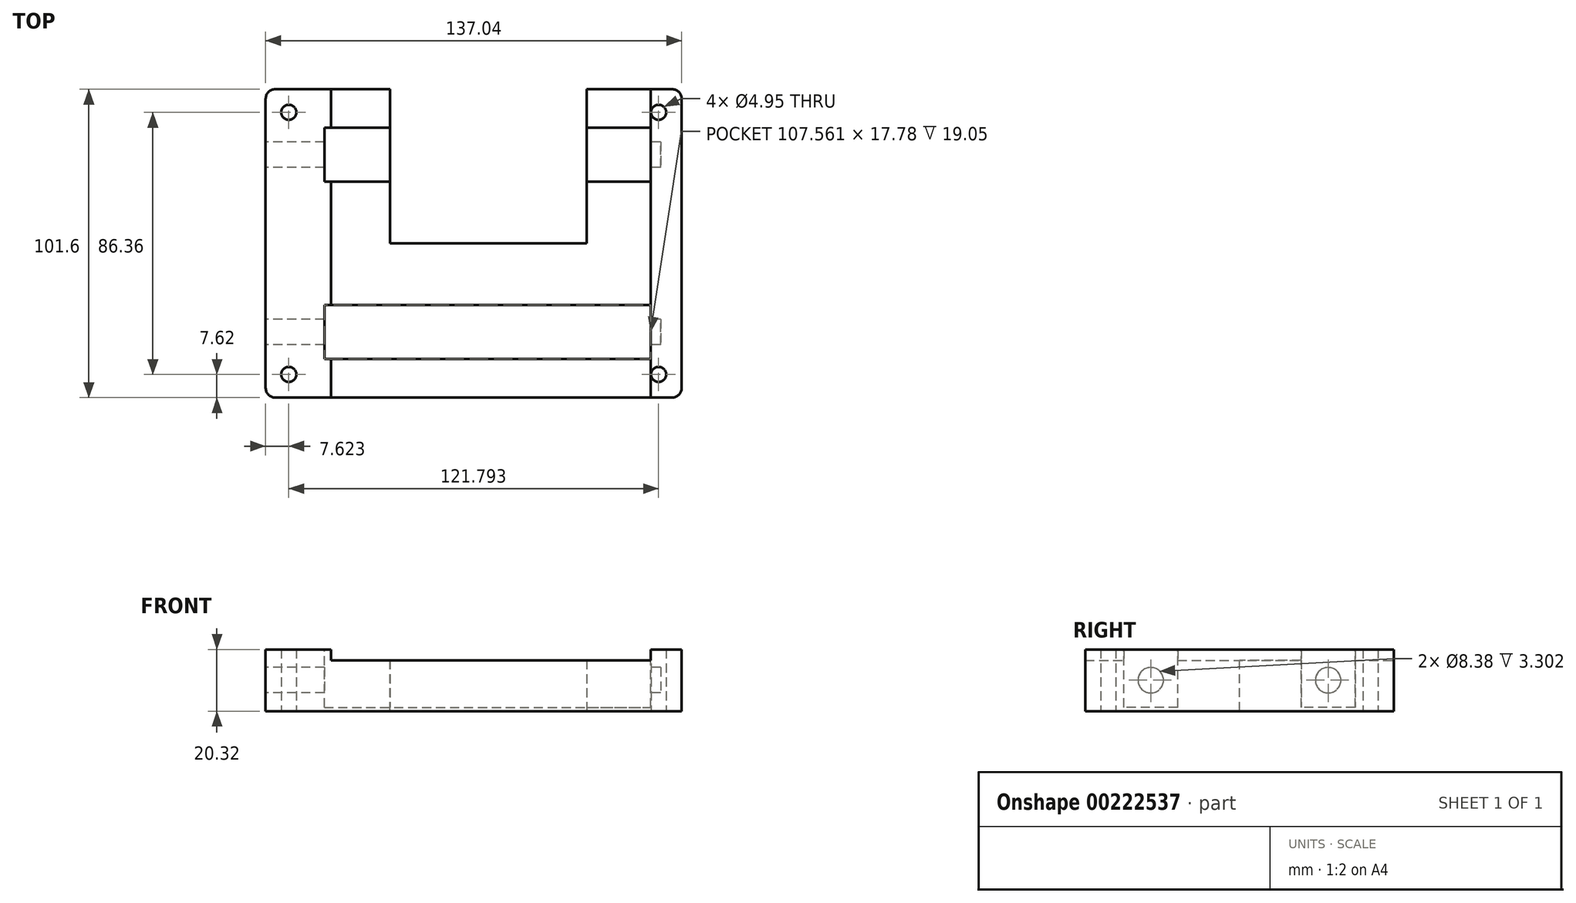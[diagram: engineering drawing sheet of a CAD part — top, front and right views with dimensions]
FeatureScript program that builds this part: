
annotation { "Feature Type Name" : "Feature", "Feature Type Description" : "" }
export const myFeature = defineFeature(function(context is Context, id is Id, definition is map)
    precondition{}
    {
        {
            var Q0;
            Q0=qCreatedBy(makeId("Right.planeOp"),FACE);
            cPlane(context, id + "F0", {"entities" : qUnion([Q0]), "cplaneType" : CPlaneType.OFFSET, "offset" : 4.83 * mm, "width" : 152.4 * mm, "height" : 152.4 * mm});
        }
        {
            var Q0;
            Q0=qCreatedBy(makeId("Top.planeOp"),FACE);
            var sketch = newSketch(context, id + "F1", { "sketchPlane" : qUnion([Q0])});
            skLineSegment(sketch, "E0", {"start": v(0, 50.8) * mm, "end": v(-68.52, 50.8) * mm});
            skLineSegment(sketch, "E1", {"start": v(-68.52, 50.8) * mm, "end": v(-68.52, 0) * mm});
            skLineSegment(sketch, "E2.MirrorCS", {"start": v(0, 50.8) * mm, "end": v(68.52, 50.8) * mm});
            skLineSegment(sketch, "E3.MirrorCS", {"start": v(68.52, 50.8) * mm, "end": v(68.52, 0) * mm});
            skLineSegment(sketch, "E4.MirrorCS", {"start": v(0, -50.8) * mm, "end": v(-68.52, -50.8) * mm});
            skLineSegment(sketch, "E5.MirrorCS", {"start": v(0, -50.8) * mm, "end": v(68.52, -50.8) * mm});
            skLineSegment(sketch, "E6.MirrorCS", {"start": v(68.52, -50.8) * mm, "end": v(68.52, 0) * mm});
            skLineSegment(sketch, "E7.MirrorCS", {"start": v(-68.52, -50.8) * mm, "end": v(-68.52, 0) * mm});
            skCircle(sketch, "E8", {"center": v(-60.9, 43.18) * mm, "radius": 2.48 * mm});
            skCircle(sketch, "E9.MirrorC", {"center": v(60.9, 43.18) * mm, "radius": 2.48 * mm});
            skCircle(sketch, "E10.MirrorC", {"center": v(-60.9, -43.18) * mm, "radius": 2.48 * mm});
            skCircle(sketch, "E11.MirrorC", {"center": v(60.9, -43.18) * mm, "radius": 2.48 * mm});
            skSolve(sketch);
        }
        {
            var Q0;
            Q0 = qSketchRegion(id + "F1", true);
            extrude(context, id + "F2", {"entities" : qUnion([Q0]), "depth" : 20.32 * mm});
        }
        {
            var Q0;
            Q0=makeQuery(id+"F2.opExtrude","SWEPT_FACE",FACE,{"disambiguationData":[OSD([sQuery(id+"F1.wireOp",EDGE,"E0"),sQuery(id+"F1.wireOp",EDGE,"E2.MirrorCS")])]});
            var sketch = newSketch(context, id + "F3", { "sketchPlane" : qUnion([Q0])});
            skLineSegment(sketch, "E12.bottom", {"start": v(-58.36, 20.32) * mm, "end": v(0, 20.32) * mm});
            skLineSegment(sketch, "E12.top", {"start": v(-58.36, 16.76) * mm, "end": v(0, 16.76) * mm});
            skLineSegment(sketch, "E12.left", {"start": v(-58.36, 20.32) * mm, "end": v(-58.36, 16.76) * mm});
            skLineSegment(sketch, "E12.right", {"start": v(0, 20.32) * mm, "end": v(0, 16.76) * mm});
            skLineSegment(sketch, "E13.bottom", {"start": v(0, 20.32) * mm, "end": v(47.04, 20.32) * mm});
            skLineSegment(sketch, "E13.top", {"start": v(0, 16.76) * mm, "end": v(47.04, 16.76) * mm});
            skLineSegment(sketch, "E13.right", {"start": v(47.04, 20.32) * mm, "end": v(47.04, 16.76) * mm});
            skSolve(sketch);
        }
        {
            var Q0;
            Q0 = qSketchRegion(id + "F3", true);
            extrude(context, id + "F4", {"entities" : qUnion([Q0]), "operationType" : NewBodyOperationType.REMOVE, "oppositeDirection" : true, "depth" : 131.57 * mm});
        }
        {
            var Q0;
            Q0=makeQuery(id+"F2.opExtrude","SWEPT_EDGE",EDGE,{"disambiguationData":[OSD([sQuery(id+"F1.wireOp",EDGE,"E2.MirrorCS"),sQuery(id+"F1.wireOp",EDGE,"E3.MirrorCS")])]});
            var Q1;
            Q1=makeQuery(id+"F2.opExtrude","SWEPT_EDGE",EDGE,{"disambiguationData":[OSD([sQuery(id+"F1.wireOp",EDGE,"E0"),sQuery(id+"F1.wireOp",EDGE,"E1")])]});
            var Q2;
            Q2=makeQuery(id+"F2.opExtrude","SWEPT_EDGE",EDGE,{"disambiguationData":[OSD([sQuery(id+"F1.wireOp",EDGE,"E4.MirrorCS"),sQuery(id+"F1.wireOp",EDGE,"E7.MirrorCS")])]});
            var Q3;
            Q3=makeQuery(id+"F2.opExtrude","SWEPT_EDGE",EDGE,{"disambiguationData":[OSD([sQuery(id+"F1.wireOp",EDGE,"E5.MirrorCS"),sQuery(id+"F1.wireOp",EDGE,"E6.MirrorCS")])]});
            fillet(context, id + "F5", {"entities" : qUnion([Q0, Q1, Q2, Q3]), "radius" : 3.17 * mm, "tangentPropagation" : true, "allowEdgeOverflow" : false});
        }
        {
            var Q0;
            Q0=qCreatedBy(id+"F0.planeOp",FACE);
            var sketch = newSketch(context, id + "F6", { "sketchPlane" : qUnion([Q0])});
            skLineSegment(sketch, "E14", {"start": v(0, 53) * mm, "end": v(0, 27.48) * mm});
            skLineSegment(sketch, "E15", {"start": v(62.4, 0) * mm, "end": v(62.4, 27.48) * mm});
            skLineSegment(sketch, "E16", {"start": v(0, 0) * mm, "end": v(62.4, 0) * mm});
            skLineSegment(sketch, "E17", {"start": v(0, 0) * mm, "end": v(0, 27.48) * mm});
            skLineSegment(sketch, "E18.trimOffspring", {"start": v(0, 0) * mm, "end": v(0, -46.74) * mm});
            skLineSegment(sketch, "E19", {"start": v(0, 27.48) * mm, "end": v(62.4, 27.48) * mm});
            skSolve(sketch);
        }
        {
            var Q0;
            Q0 = qSketchRegion(id + "F6", true);
            extrude(context, id + "F7", {"entities" : qUnion([Q0]), "operationType" : NewBodyOperationType.REMOVE, "endBound" : BoundingType.SYMMETRIC, "oppositeDirection" : true, "depth" : 64.77 * mm});
        }
        {
            var Q0;
            {var subQ0=sQuery(id+"F1.wireOp",EDGE,"E2.MirrorCS");var subQ1=sQuery(id+"F1.wireOp",EDGE,"E0");var subQ2=sQuery(id+"F1.wireOp",EDGE,"E7.MirrorCS");var subQ3=sQuery(id+"F1.wireOp",EDGE,"E1");var subQ4=sQuery(id+"F1.wireOp",EDGE,"E5.MirrorCS");var subQ5=sQuery(id+"F1.wireOp",EDGE,"E4.MirrorCS");Q0=makeQuery(id+"F4.boolean.opBoolean","SPLIT",FACE,{"disambiguationData":[TD([makeQuery(id+"F4.opExtrude","SWEPT_FACE",FACE,{"disambiguationData":[OSD([sQuery(id+"F3.wireOp",EDGE,"E13.right")])]})])],"derivedFrom":makeQuery(id+"F2.opExtrude","CAP_FACE",FACE,{"disambiguationData":[OSD([subQ1,subQ3,subQ0,sQuery(id+"F1.wireOp",EDGE,"E3.MirrorCS"),subQ5,subQ4,sQuery(id+"F1.wireOp",EDGE,"E6.MirrorCS"),subQ2])],"isStart":false})});}
            var sketch = newSketch(context, id + "F8", { "sketchPlane" : qUnion([Q0])});
            skLineSegment(sketch, "E20.bottom", {"start": v(-49.2, 38.1) * mm, "end": v(0, 38.1) * mm});
            skLineSegment(sketch, "E20.top", {"start": v(-49.2, 20.32) * mm, "end": v(0, 20.32) * mm});
            skLineSegment(sketch, "E20.left", {"start": v(-49.2, 38.1) * mm, "end": v(-49.2, 20.32) * mm});
            skLineSegment(sketch, "E20.right", {"start": v(0, 38.1) * mm, "end": v(0, 20.32) * mm});
            skLineSegment(sketch, "E21.bottom", {"start": v(0, 38.1) * mm, "end": v(58.36, 38.1) * mm});
            skLineSegment(sketch, "E21.top", {"start": v(0, 20.32) * mm, "end": v(58.36, 20.32) * mm});
            skLineSegment(sketch, "E21.right", {"start": v(58.36, 38.1) * mm, "end": v(58.36, 20.32) * mm});
            skLineSegment(sketch, "E22.bottom", {"start": v(-49.2, -20.32) * mm, "end": v(58.36, -20.32) * mm});
            skLineSegment(sketch, "E22.top", {"start": v(-49.2, -38.1) * mm, "end": v(58.36, -38.1) * mm});
            skLineSegment(sketch, "E22.left", {"start": v(-49.2, -20.32) * mm, "end": v(-49.2, -38.1) * mm});
            skLineSegment(sketch, "E22.right", {"start": v(58.36, -20.32) * mm, "end": v(58.36, -38.1) * mm});
            skSolve(sketch);
        }
        {
            var Q0;
            Q0 = qSketchRegion(id + "F8", true);
            extrude(context, id + "F9", {"entities" : qUnion([Q0]), "operationType" : NewBodyOperationType.REMOVE, "oppositeDirection" : true, "depth" : 19.05 * mm});
        }
        {
            var Q0;
            Q0=makeQuery(id+"F2.opExtrude","SWEPT_FACE",FACE,{"disambiguationData":[OSD([sQuery(id+"F1.wireOp",EDGE,"E1"),sQuery(id+"F1.wireOp",EDGE,"E7.MirrorCS")])]});
            var sketch = newSketch(context, id + "F10", { "sketchPlane" : qUnion([Q0])});
            skCircle(sketch, "E23", {"center": v(-29.21, 10.2) * mm, "radius": 4.2 * mm});
            skCircle(sketch, "E24", {"center": v(29.21, 10.2) * mm, "radius": 4.2 * mm});
            skSolve(sketch);
        }
        {
            var Q0;
            Q0 = qSketchRegion(id + "F10", true);
            extrude(context, id + "F11", {"entities" : qUnion([Q0]), "operationType" : NewBodyOperationType.REMOVE, "oppositeDirection" : true, "depth" : 130.17 * mm});
        }
    });
